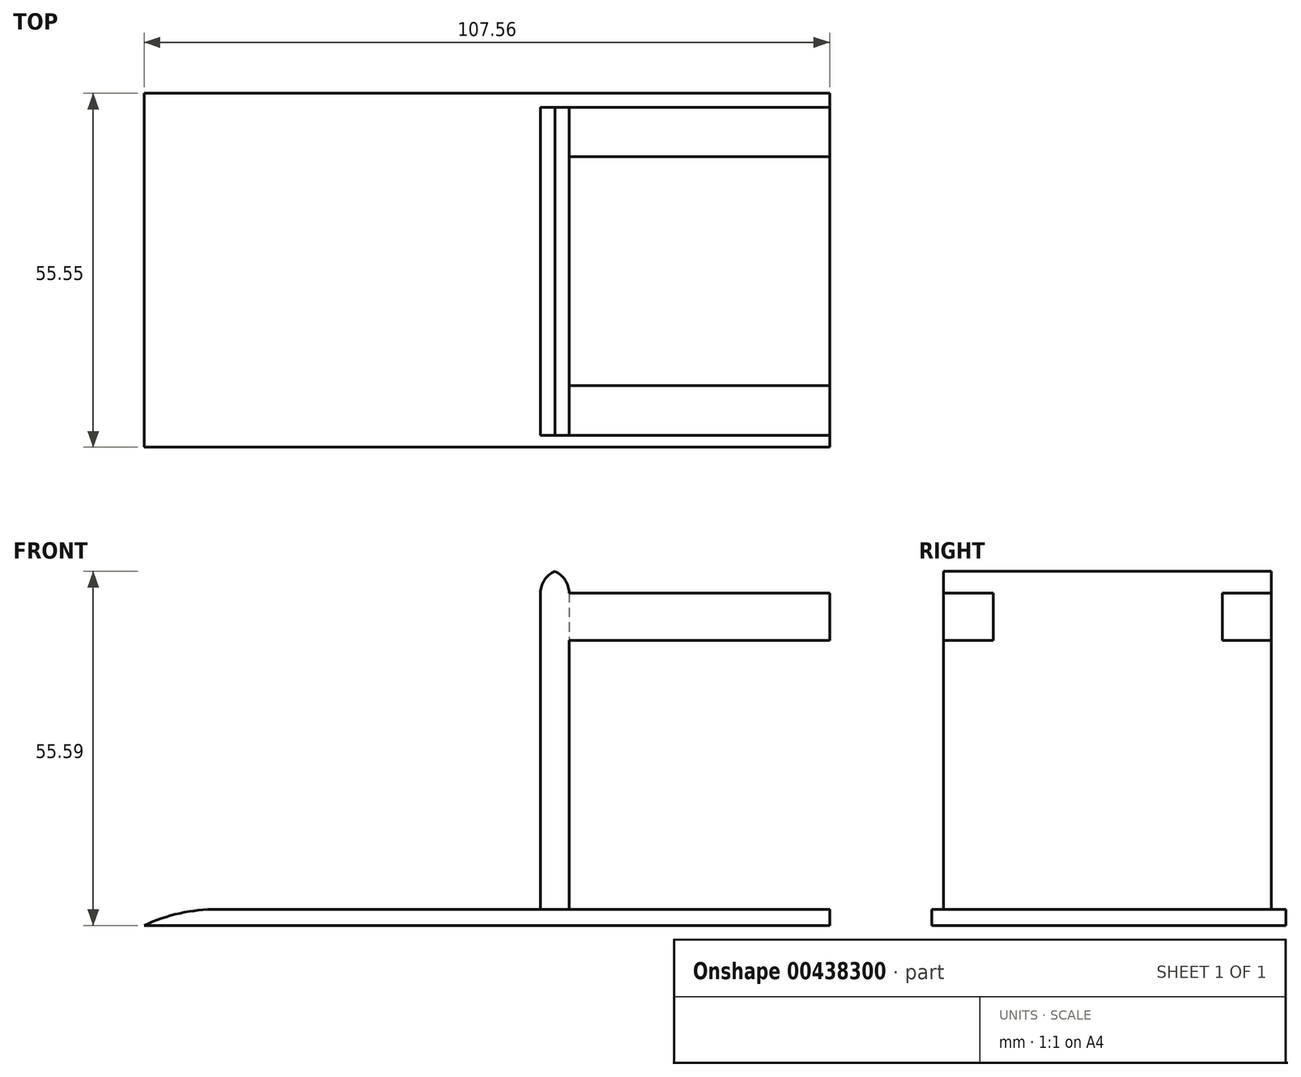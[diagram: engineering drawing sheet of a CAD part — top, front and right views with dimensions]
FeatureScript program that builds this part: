
annotation { "Feature Type Name" : "Feature", "Feature Type Description" : "" }
export const myFeature = defineFeature(function(context is Context, id is Id, definition is map)
    precondition{}
    {
        {
            var Q0;
            Q0=qCreatedBy(makeId("Top.planeOp"),FACE);
            var sketch = newSketch(context, id + "F0", { "sketchPlane" : qUnion([Q0])});
            skLineSegment(sketch, "E0.bottom", {"start": v(0, 0) * mm, "end": v(-68.19, 0) * mm});
            skLineSegment(sketch, "E0.top", {"start": v(0, 55.55) * mm, "end": v(-68.19, 55.55) * mm});
            skLineSegment(sketch, "E0.left", {"start": v(0, 0) * mm, "end": v(0, 55.55) * mm});
            skLineSegment(sketch, "E0.right", {"start": v(-68.19, 0) * mm, "end": v(-68.19, 55.55) * mm});
            skSolve(sketch);
        }
        {
            var Q0;
            Q0=makeQuery(id+"F0.imprint","IMPRINT",FACE,{"disambiguationData":[TD([[makeQuery(id+"F0.imprint","IMPRINT",EDGE,{"derivedFrom":sQuery(id+"F0.wireOp",EDGE,"E0.bottom")}),-1.0]])]});
            extrude(context, id + "F1", {"entities" : qUnion([Q0]), "depth" : 2.54 * mm});
        }
        {
            var Q0;
            Q0=makeQuery(id+"F1.opExtrude","CAP_EDGE",EDGE,{"disambiguationData":[OSD([sQuery(id+"F0.wireOp",EDGE,"E0.right")])],"isStart":false});
            fillet(context, id + "F2", {"entities" : qUnion([Q0]), "radius" : 26.98 * mm, "tangentPropagation" : true, "allowEdgeOverflow" : false});
        }
        {
            var Q0;
            Q0=makeQuery(id+"F1.opExtrude","CAP_FACE",FACE,{"disambiguationData":[OSD([sQuery(id+"F0.wireOp",EDGE,"E0.bottom"),sQuery(id+"F0.wireOp",EDGE,"E0.top"),sQuery(id+"F0.wireOp",EDGE,"E0.left"),sQuery(id+"F0.wireOp",EDGE,"E0.right")])],"isStart":false});
            var sketch = newSketch(context, id + "F3", { "sketchPlane" : qUnion([Q0])});
            skLineSegment(sketch, "E1.bottom", {"start": v(-1.52, 1.84) * mm, "end": v(-6, 1.84) * mm});
            skLineSegment(sketch, "E1.top", {"start": v(-1.52, 53.32) * mm, "end": v(-6, 53.32) * mm});
            skLineSegment(sketch, "E1.left", {"start": v(-1.52, 1.84) * mm, "end": v(-1.52, 53.32) * mm});
            skLineSegment(sketch, "E1.right", {"start": v(-6, 1.84) * mm, "end": v(-6, 53.32) * mm});
            skSolve(sketch);
        }
        {
            var Q0;
            Q0=makeQuery(id+"F3.imprint","IMPRINT",FACE,{"disambiguationData":[TD([[makeQuery(id+"F3.imprint","IMPRINT",EDGE,{"derivedFrom":sQuery(id+"F3.wireOp",EDGE,"E1.bottom")}),-1.0]])]});
            extrude(context, id + "F4", {"entities" : qUnion([Q0]), "operationType" : NewBodyOperationType.ADD, "depth" : 53.34 * mm});
        }
        {
            var Q0;
            Q0=makeQuery(id+"F4.opExtrude","CAP_EDGE",EDGE,{"disambiguationData":[OSD([sQuery(id+"F3.wireOp",EDGE,"E1.left")])],"isStart":false});
            var Q1;
            Q1=makeQuery(id+"F4.opExtrude","CAP_EDGE",EDGE,{"disambiguationData":[OSD([sQuery(id+"F3.wireOp",EDGE,"E1.right")])],"isStart":false});
            fillet(context, id + "F5", {"entities" : qUnion([Q0, Q1]), "radius" : 3.68 * mm, "tangentPropagation" : true, "allowEdgeOverflow" : false});
        }
        {
            var Q0;
            Q0=makeQuery(id+"F4.opExtrude","SWEPT_FACE",FACE,{"disambiguationData":[OSD([sQuery(id+"F3.wireOp",EDGE,"E1.left")])]});
            var sketch = newSketch(context, id + "F6", { "sketchPlane" : qUnion([Q0])});
            skLineSegment(sketch, "E2.bottom", {"start": v(1.84, 52.2) * mm, "end": v(9.65, 52.2) * mm});
            skLineSegment(sketch, "E2.top", {"start": v(1.84, 44.73) * mm, "end": v(9.65, 44.73) * mm});
            skLineSegment(sketch, "E2.left", {"start": v(1.84, 52.2) * mm, "end": v(1.84, 44.73) * mm});
            skLineSegment(sketch, "E2.right", {"start": v(9.65, 52.2) * mm, "end": v(9.65, 44.73) * mm});
            skLineSegment(sketch, "E3.bottom", {"start": v(53.32, 52.2) * mm, "end": v(45.6, 52.2) * mm});
            skLineSegment(sketch, "E3.top", {"start": v(53.32, 44.73) * mm, "end": v(45.6, 44.73) * mm});
            skLineSegment(sketch, "E3.left", {"start": v(53.32, 52.2) * mm, "end": v(53.32, 44.73) * mm});
            skLineSegment(sketch, "E3.right", {"start": v(45.6, 52.2) * mm, "end": v(45.6, 44.73) * mm});
            skSolve(sketch);
        }
        {
            var Q0;
            Q0=makeQuery(id+"F6.imprint","IMPRINT",FACE,{"disambiguationData":[TD([[makeQuery(id+"F6.imprint","IMPRINT",EDGE,{"derivedFrom":sQuery(id+"F6.wireOp",EDGE,"E2.bottom")}),1.0]])]});
            var Q1;
            Q1=makeQuery(id+"F6.imprint","IMPRINT",FACE,{"disambiguationData":[TD([[makeQuery(id+"F6.imprint","IMPRINT",EDGE,{"derivedFrom":sQuery(id+"F6.wireOp",EDGE,"E3.bottom")}),1.0]])]});
            extrude(context, id + "F7", {"entities" : qUnion([Q0, Q1]), "operationType" : NewBodyOperationType.ADD, "depth" : 40.9 * mm});
        }
        {
            var Q0;
            Q0=makeQuery(id+"F1.opExtrude","SWEPT_FACE",FACE,{"disambiguationData":[OSD([sQuery(id+"F0.wireOp",EDGE,"E0.left")])]});
            extrude(context, id + "F8", {"entities" : qUnion([Q0]), "operationType" : NewBodyOperationType.ADD, "depth" : 39.37 * mm});
        }
    });
